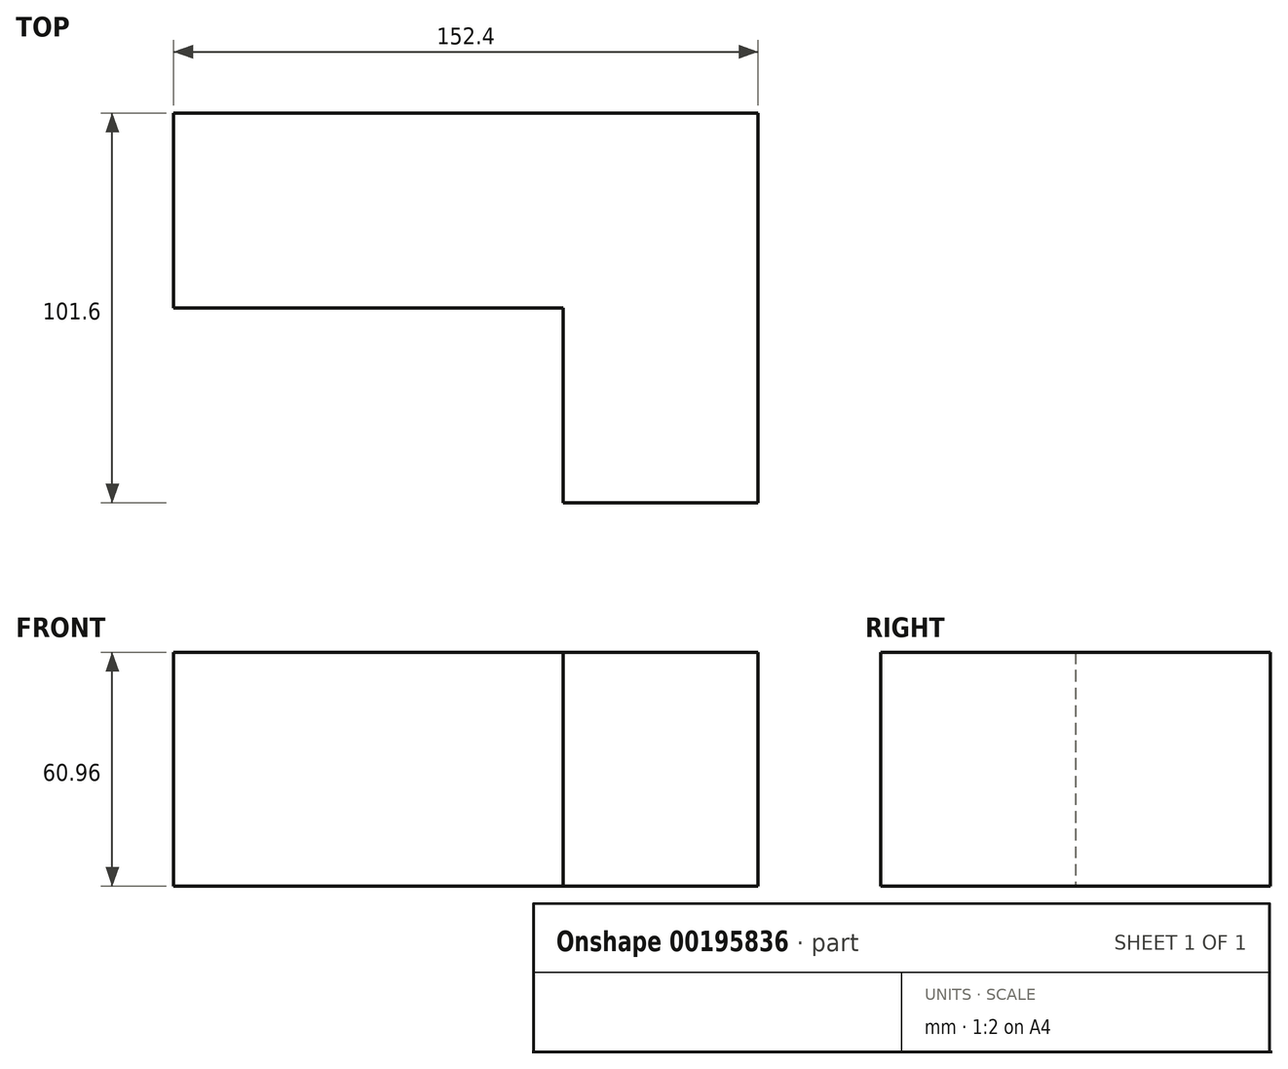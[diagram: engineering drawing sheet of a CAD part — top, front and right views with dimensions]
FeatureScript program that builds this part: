
annotation { "Feature Type Name" : "Feature", "Feature Type Description" : "" }
export const myFeature = defineFeature(function(context is Context, id is Id, definition is map)
    precondition{}
    {
        {
            var Q0;
            Q0=qCreatedBy(makeId("Top.planeOp"),FACE);
            var sketch = newSketch(context, id + "F0", { "sketchPlane" : qUnion([Q0])});
            skLineSegment(sketch, "E0.bottom", {"start": v(-76.2, 50.8) * mm, "end": v(76.2, 50.8) * mm});
            skLineSegment(sketch, "E0.top", {"start": v(-76.2, -50.8) * mm, "end": v(76.2, -50.8) * mm});
            skLineSegment(sketch, "E0.left", {"start": v(-76.2, 50.8) * mm, "end": v(-76.2, -50.8) * mm});
            skLineSegment(sketch, "E0.right", {"start": v(76.2, 50.8) * mm, "end": v(76.2, -50.8) * mm});
            skPoint(sketch, "E0.middle", {"position": v(0, 0) * mm});
            skLineSegment(sketch, "E1.bottom", {"start": v(-76.2, -50.8) * mm, "end": v(25.4, -50.8) * mm});
            skLineSegment(sketch, "E1.top", {"start": v(-76.2, 0) * mm, "end": v(25.4, 0) * mm});
            skLineSegment(sketch, "E1.left", {"start": v(-76.2, -50.8) * mm, "end": v(-76.2, 0) * mm});
            skLineSegment(sketch, "E1.right", {"start": v(25.4, -50.8) * mm, "end": v(25.4, 0) * mm});
            skSolve(sketch);
        }
        {
            var Q0;
            Q0=makeQuery(id+"F0.imprint","IMPRINT",FACE,{"disambiguationData":[TD([[makeQuery(id+"F0.imprint","IMPRINT",EDGE,{"derivedFrom":sQuery(id+"F0.wireOp",EDGE,"E0.bottom")}),-1.0]])]});
            extrude(context, id + "F1", {"entities" : qUnion([Q0]), "depth" : 60.96 * mm});
        }
    });
